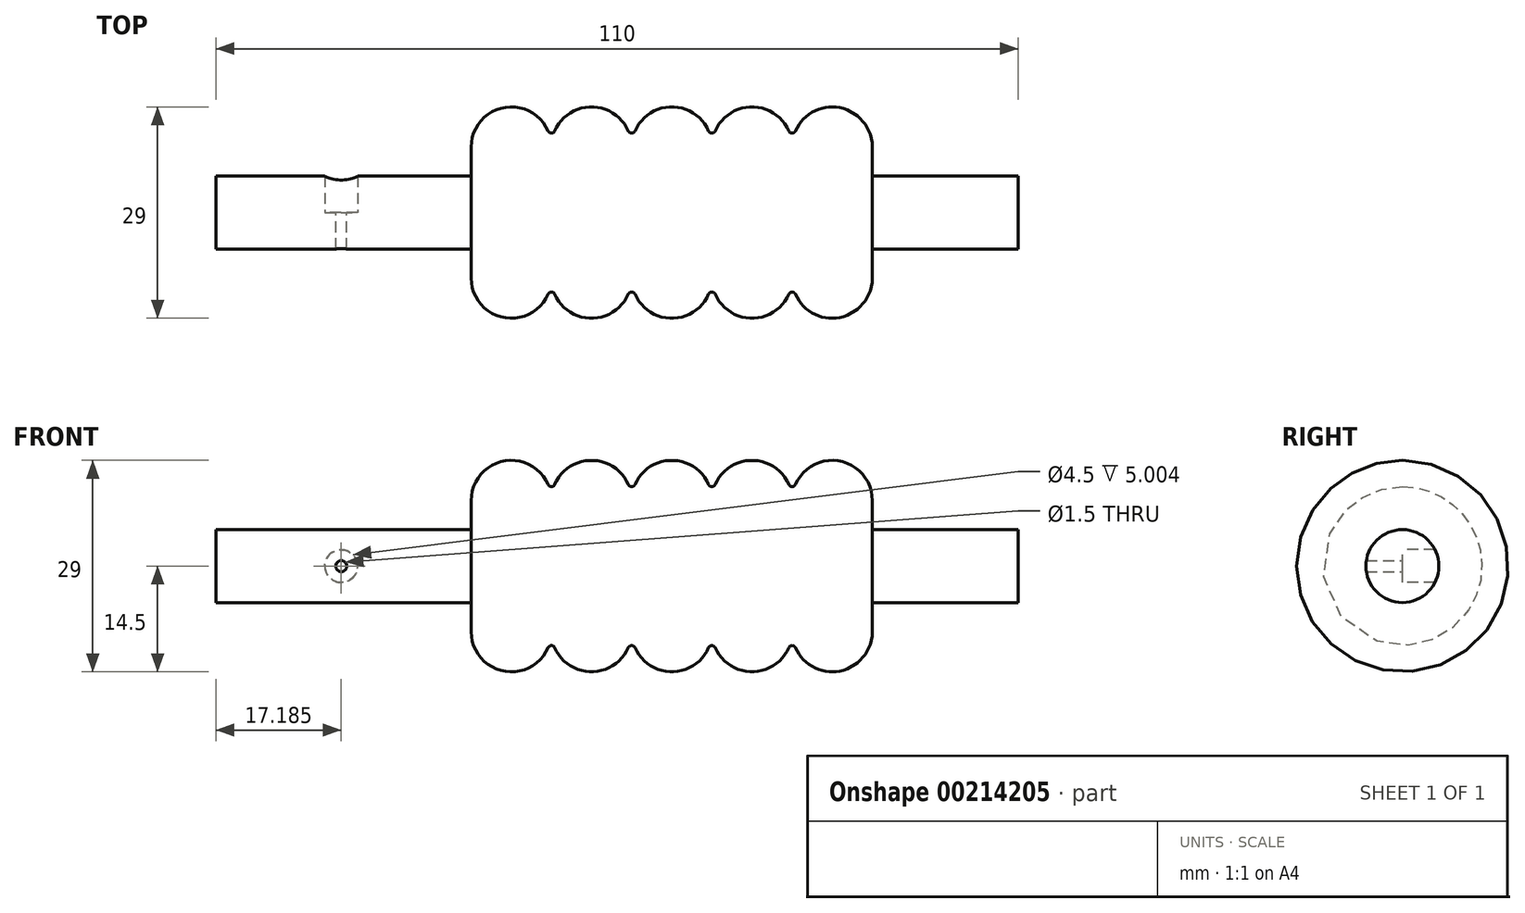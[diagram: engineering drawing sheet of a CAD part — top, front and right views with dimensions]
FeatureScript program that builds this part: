
annotation { "Feature Type Name" : "Feature", "Feature Type Description" : "" }
export const myFeature = defineFeature(function(context is Context, id is Id, definition is map)
    precondition{}
    {
        {
            var Q0;
            Q0=qCreatedBy(makeId("Front.planeOp"),FACE);
            var sketch = newSketch(context, id + "F0", { "sketchPlane" : qUnion([Q0])});
            skLineSegment(sketch, "E0", {"start": v(-110, 0) * mm, "end": v(103.89, 0) * mm});
            skLineSegment(sketch, "E1", {"start": v(-110, 0) * mm, "end": v(-110, 5) * mm});
            skLineSegment(sketch, "E2", {"start": v(-110, 5) * mm, "end": v(-75, 5) * mm});
            skLineSegment(sketch, "E3", {"start": v(-75, 5) * mm, "end": v(-75, 9) * mm});
            skArc(sketch, "E4", {"start": v(-64.46, 11.2) * mm, "mid": v(-70.62, 14.38) * mm, "end": v(-75, 9) * mm});
            skLineSegment(sketch, "E5", {"start": v(-75, 9) * mm, "end": v(5.66, 9) * mm, "construction": true});
            skArc(sketch, "E6.1.0.0", {"start": v(-53.46, 11.2) * mm, "mid": v(-58.5, 14.5) * mm, "end": v(-63.54, 11.2) * mm});
            skArc(sketch, "E6.2.0.0", {"start": v(-42.46, 11.2) * mm, "mid": v(-47.5, 14.5) * mm, "end": v(-52.54, 11.2) * mm});
            skArc(sketch, "E6.3.0.0", {"start": v(-31.46, 11.2) * mm, "mid": v(-36.5, 14.5) * mm, "end": v(-41.54, 11.2) * mm});
            skArc(sketch, "E6.4.0.0", {"start": v(-20, 9) * mm, "mid": v(-24.38, 14.38) * mm, "end": v(-30.54, 11.2) * mm});
            skLineSegment(sketch, "E6.direction1", {"start": v(-75, 9) * mm, "end": v(-65, 9) * mm, "construction": true});
            skPoint(sketch, "E7.visualSharp", {"position": v(-64, 9) * mm});
            skArc(sketch, "E7.filletArc", {"start": v(-64.46, 11.2) * mm, "mid": v(-64, 10.9) * mm, "end": v(-63.54, 11.2) * mm});
            skPoint(sketch, "E8.visualSharp", {"position": v(-53, 9) * mm});
            skArc(sketch, "E8.filletArc", {"start": v(-53.46, 11.2) * mm, "mid": v(-53, 10.9) * mm, "end": v(-52.54, 11.2) * mm});
            skPoint(sketch, "E9.visualSharp", {"position": v(-42, 9) * mm});
            skArc(sketch, "E9.filletArc", {"start": v(-42.46, 11.2) * mm, "mid": v(-42, 10.9) * mm, "end": v(-41.54, 11.2) * mm});
            skPoint(sketch, "E10.visualSharp", {"position": v(-31, 9) * mm});
            skArc(sketch, "E10.filletArc", {"start": v(-31.46, 11.2) * mm, "mid": v(-31, 10.9) * mm, "end": v(-30.54, 11.2) * mm});
            skLineSegment(sketch, "E11", {"start": v(-20, 9) * mm, "end": v(-20, 5) * mm});
            skLineSegment(sketch, "E12", {"start": v(-20, 5) * mm, "end": v(0, 5) * mm});
            skLineSegment(sketch, "E13", {"start": v(0, 5) * mm, "end": v(0, 0) * mm});
            skLineSegment(sketch, "E14", {"start": v(-69.5, 0) * mm, "end": v(-69.5, 14.5) * mm, "construction": true});
            skSolve(sketch);
        }
        {
            var Q0;
            Q0 = qSketchRegion(id + "F0", true);
            var Q1;
            Q1=sQuery(id+"F0.wireOp",EDGE,"E0");
            revolve(context, id + "F1", {"entities" : qUnion([Q0]), "axis" : qUnion([Q1]), "revolveType" : RevolveType.FULL});
        }
        {
            var Q0;
            Q0=qCreatedBy(makeId("Front.planeOp"),FACE);
            var sketch = newSketch(context, id + "F2", { "sketchPlane" : qUnion([Q0])});
            skCircle(sketch, "E15", {"center": v(-92.81, 0) * mm, "radius": 2.25 * mm});
            skCircle(sketch, "E16", {"center": v(-92.81, 0) * mm, "radius": 0.75 * mm});
            skSolve(sketch);
        }
        {
            var Q0;
            Q0 = qSketchRegion(id + "F2", true);
            extrude(context, id + "F3", {"entities" : qUnion([Q0]), "operationType" : NewBodyOperationType.REMOVE, "oppositeDirection" : true, "depth" : 25 * mm, "offsetDistance" : 25 * mm});
        }
        {
            var Q0;
            Q0=makeQuery(id+"F2.imprint","IMPRINT",FACE,{"disambiguationData":[TD([[makeQuery(id+"F2.imprint","IMPRINT",EDGE,{"derivedFrom":sQuery(id+"F2.wireOp",EDGE,"E16")}),1.0]])]});
            extrude(context, id + "F4", {"entities" : qUnion([Q0]), "operationType" : NewBodyOperationType.REMOVE, "depth" : 25 * mm, "offsetDistance" : 25 * mm, "hasSecondDirection" : true, "secondDirectionOppositeDirection" : true, "secondDirectionDepth" : 25 * mm});
        }
    });
